# Revit family: OPA_820_Econex_Pro_1024
name_source: partatom
category: Mechanical Equipment
units: mm (PartAtom-declared; Revit-internal decimal feet)

## family parameters
Always vertical = Yes
Cut with Voids When Loaded = Yes
Maintain Annotation Orientation = No
OmniClass Number = 23.75.35.14
OmniClass Title = Air Handling Units
Part Type = Normal
Room Calculation Point = No
Round Connector Dimension = Use Radius
Shared = No
Work Plane-Based = No

## types (6) — shared parameters
Clearance Zones = Clearance Zones
Condensate Drain = Condensate Drain - 1"BSP Female
CondensorFanDiameter = 890 mm  [stored 2.91995 ft]
CondensorFanHeight = 301 mm  [stored 0.987533 ft]
Cooling capacity range (gross) = 11.2 ~ 88.3 kW
Drainage = 17 mm
DrainageLeftOffset = 1054 mm
Finish = Grey Polyester Powder Coat
Heating capacity range = 10.0 ~ 97.0 kW
HeatingCapacity = 81.4 kW
Indoor Fan Full Load Amps = 4.5 A/ph (x2)
Manufacturer = temperzone ltd
Max Running Amps_Total System = 55 / 50 / 66 A
ModifiedIssue_ANZRS = 240801.01 $
MountingPointLength = 2831 mm  [stored 9.28806 ft]
MountingPointWidth = 1967 mm  [stored 6.45341 ft]
NOTE = Models are representative of actual units, for exact model details please contact your Temperzone representative
NetCoolingCapacity = 80.2 kW
Nett Weight = 1,270 kg
Nominal Airflow = 4300.0 L/s
Power Source = 3 ph. 400 V ac 50 Hz + N + E
Running Amps_Total System = 37 / 39 / 45 A
TCSPF (cold/mixed/hot) = 5.175 / 4.669 / 4.506
Type Comments = The manufacturer reserves the right to change specifications at any time without notice or obligation. Certified dimensions available on request.
URL = www.temperzone.com
UnitHeight = 1957 mm  [stored 6.4206 ft]
UnitLength = 2808 mm  [stored 9.2126 ft]
UnitWidth = 2107 mm  [stored 6.91273 ft]
Voltage = 400 V
WHBaseWidth = 671 mm  [stored 2.20144 ft]
WHEndWidth = 1337 mm  [stored 4.38648 ft]
WHHeight = 1491 mm  [stored 4.89173 ft]
WHMedDepth = 245 mm  [stored 0.803806 ft]
WHTotalDepth = 606 mm  [stored 1.98819 ft]
WeatherHoodBackOffset = 1592 mm  [stored 5.2231 ft]
WeatherHoodVerticalOffset = 401 mm  [stored 1.31562 ft]
zero-valued in all types: Default Elevation

## per-type parameters (varying)
| type | Model | RSRotationOwnAxis | RSpigotDepth | RSpigotHeight | RSpigotVerticalAngle | RSpigotWidth | ReturnSpigotBackOffset | ReturnSpigotLeftOffset | ReturnSpigotVerticalOffset | SSRotationOwnAxis | SSpigotDepth | SSpigotHeight | SSpigotVerticalAngle | SSpigotWidth | SupplySpigotBackOffset | SupplySpigotLeftOffset | SupplySpigotVerticalOffset | WHHorizontalAngle | WeatherHoodLeftOffset |
| OPA 820 Econex Pro (StdHand_Downward) | OPA 820RLTB1FPQ23 (StdHand_Downward) | 90.00° | 109 mm  [stored 0.357612 ft] | 1166 mm | 0.00° | 550 mm | 1996 mm | 1655 mm  [stored 5.42979 ft] | 123 mm  [stored 0.403543 ft] | 90.00° | 109 mm  [stored 0.357612 ft] | 1166 mm | 0.00° | 550 mm | 1996 mm | 451 mm  [stored 1.47966 ft] | 123 mm  [stored 0.403543 ft] | 0.00° | 2107 mm  [stored 6.91273 ft] |
| OPA 820 Econex Pro (OppHand_Horizontal) | OPA 820RLTB1FPQ10 (OppHand_Horizontal) | 270.00° | 50 mm  [stored 0.164042 ft] | 1200 mm  [stored 3.93701 ft] | 90.00° | 600 mm | 2808 mm  [stored 9.2126 ft] | 425 mm  [stored 1.39436 ft] | 971 mm  [stored 3.1857 ft] | 270.00° | 50 mm  [stored 0.164042 ft] | 1200 mm  [stored 3.93701 ft] | 90.00° | 600 mm | 2808 mm  [stored 9.2126 ft] | 1682 mm  [stored 5.51837 ft] | 971 mm  [stored 3.1857 ft] | 180.00° | 0 mm  [stored 0 ft] |
| OPA 820 Econex Pro (OppHand_Downward) | OPA 820RLTB1FPQ32 (OppHand_Downward) | 270.00° | 109 mm  [stored 0.357612 ft] | 1166 mm | 0.00° | 550 mm | 1996 mm | 451 mm  [stored 1.47966 ft] | 123 mm  [stored 0.403543 ft] | 270.00° | 109 mm  [stored 0.357612 ft] | 1166 mm | 0.00° | 550 mm | 1996 mm | 1655 mm  [stored 5.42979 ft] | 123 mm  [stored 0.403543 ft] | 180.00° | 0 mm  [stored 0 ft] |
| OPA 820 Econex Pro (StdHand_Horizontal) | OPA 820RLTB1FPQ01 (StdHand_Horizontal) | 90.00° | 50 mm  [stored 0.164042 ft] | 1200 mm  [stored 3.93701 ft] | 90.00° | 600 mm | 2808 mm  [stored 9.2126 ft] | 1682 mm  [stored 5.51837 ft] | 971 mm  [stored 3.1857 ft] | 90.00° | 50 mm  [stored 0.164042 ft] | 1200 mm  [stored 3.93701 ft] | 90.00° | 600 mm | 2808 mm  [stored 9.2126 ft] | 425 mm  [stored 1.39436 ft] | 971 mm  [stored 3.1857 ft] | 0.00° | 2107 mm  [stored 6.91273 ft] |
| OPA 820 Econex Pro (StdHand_Upward) | OPA 820RLTB1FPQ45 (StdHand_Upward) | 90.00° | 60 mm  [stored 0.19685 ft] | 1225 mm  [stored 4.01903 ft] | 180.00° | 615 mm  [stored 2.01772 ft] | 1987 mm | 1686 mm  [stored 5.5315 ft] | 1957 mm  [stored 6.4206 ft] | 90.00° | 60 mm  [stored 0.19685 ft] | 1225 mm  [stored 4.01903 ft] | 180.00° | 615 mm  [stored 2.01772 ft] | 1987 mm | 421 mm  [stored 1.38123 ft] | 1957 mm  [stored 6.4206 ft] | 0.00° | 2107 mm  [stored 6.91273 ft] |
| OPA 820 Econex Pro (OppHand_Upward) | OPA 820RLTB1FPQ54 (OppHand_Upward) | 270.00° | 60 mm  [stored 0.19685 ft] | 1225 mm  [stored 4.01903 ft] | 180.00° | 615 mm  [stored 2.01772 ft] | 1987 mm | 421 mm  [stored 1.38123 ft] | 1957 mm  [stored 6.4206 ft] | 270.00° | 60 mm  [stored 0.19685 ft] | 1225 mm  [stored 4.01903 ft] | 180.00° | 615 mm  [stored 2.01772 ft] | 1987 mm | 1686 mm  [stored 5.5315 ft] | 1957 mm  [stored 6.4206 ft] | 180.00° | 0 mm  [stored 0 ft] |

note: [stored X ft] marks values corroborated as IEEE doubles in the binary element streams (Revit-internal decimal feet)

## geometry (parser evidence)
native form markers: Sweep x14
no freeform markers — native parametric forms only
